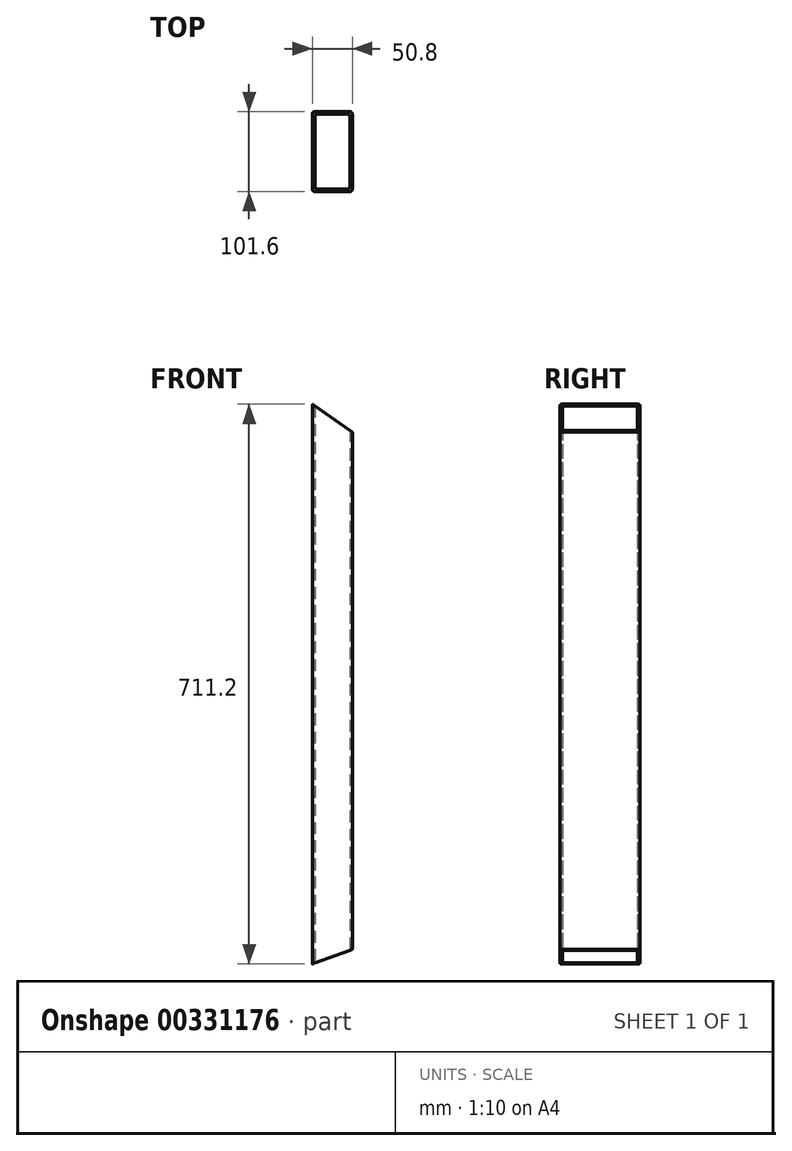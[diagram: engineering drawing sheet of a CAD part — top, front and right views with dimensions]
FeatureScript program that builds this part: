
annotation { "Feature Type Name" : "Feature", "Feature Type Description" : "" }
export const myFeature = defineFeature(function(context is Context, id is Id, definition is map)
    precondition{}
    {
        {
            var Q0;
            Q0=qCreatedBy(makeId("Top.planeOp"),FACE);
            var sketch = newSketch(context, id + "F0", { "sketchPlane" : qUnion([Q0])});
            skLineSegment(sketch, "E0.bottom", {"start": v(22.23, -50.8) * mm, "end": v(-22.22, -50.8) * mm});
            skLineSegment(sketch, "E0.top", {"start": v(22.22, 50.8) * mm, "end": v(-22.23, 50.8) * mm});
            skLineSegment(sketch, "E0.left", {"start": v(25.4, -47.62) * mm, "end": v(25.4, 47.63) * mm});
            skLineSegment(sketch, "E0.right", {"start": v(-25.4, -47.62) * mm, "end": v(-25.4, 47.63) * mm});
            skPoint(sketch, "E0.middle", {"position": v(0, 0) * mm});
            skLineSegment(sketch, "E1.bottom", {"start": v(19.05, -47.62) * mm, "end": v(-19.05, -47.63) * mm});
            skLineSegment(sketch, "E1.top", {"start": v(19.05, 47.63) * mm, "end": v(-19.05, 47.62) * mm});
            skLineSegment(sketch, "E1.left", {"start": v(22.23, -44.45) * mm, "end": v(22.22, 44.45) * mm});
            skLineSegment(sketch, "E1.right", {"start": v(-22.22, -44.45) * mm, "end": v(-22.23, 44.45) * mm});
            skPoint(sketch, "E2.visualSharp", {"position": v(-22.23, 47.62) * mm});
            skArc(sketch, "E2.filletArc", {"start": v(-19.05, 47.62) * mm, "mid": v(-21.3, 46.7) * mm, "end": v(-22.23, 44.45) * mm});
            skPoint(sketch, "E3.visualSharp", {"position": v(-25.4, 50.8) * mm});
            skArc(sketch, "E3.filletArc", {"start": v(-22.23, 50.8) * mm, "mid": v(-24.47, 49.87) * mm, "end": v(-25.4, 47.63) * mm});
            skPoint(sketch, "E4.visualSharp", {"position": v(22.22, 47.63) * mm});
            skArc(sketch, "E4.filletArc", {"start": v(22.22, 44.45) * mm, "mid": v(21.3, 46.7) * mm, "end": v(19.05, 47.63) * mm});
            skPoint(sketch, "E5.visualSharp", {"position": v(25.4, 50.8) * mm});
            skArc(sketch, "E5.filletArc", {"start": v(25.4, 47.63) * mm, "mid": v(24.47, 49.87) * mm, "end": v(22.22, 50.8) * mm});
            skPoint(sketch, "E6.visualSharp", {"position": v(-22.22, -47.63) * mm});
            skArc(sketch, "E6.filletArc", {"start": v(-22.22, -44.45) * mm, "mid": v(-21.3, -46.7) * mm, "end": v(-19.05, -47.63) * mm});
            skPoint(sketch, "E7.visualSharp", {"position": v(22.23, -47.62) * mm});
            skArc(sketch, "E7.filletArc", {"start": v(19.05, -47.62) * mm, "mid": v(21.3, -46.7) * mm, "end": v(22.23, -44.45) * mm});
            skPoint(sketch, "E8.visualSharp", {"position": v(25.4, -50.8) * mm});
            skArc(sketch, "E8.filletArc", {"start": v(22.23, -50.8) * mm, "mid": v(24.47, -49.87) * mm, "end": v(25.4, -47.62) * mm});
            skPoint(sketch, "E9.visualSharp", {"position": v(-25.4, -50.8) * mm});
            skArc(sketch, "E9.filletArc", {"start": v(-25.4, -47.62) * mm, "mid": v(-24.47, -49.87) * mm, "end": v(-22.22, -50.8) * mm});
            skSolve(sketch);
        }
        {
            var Q0;
            Q0 = qSketchRegion(id + "F0", true);
            extrude(context, id + "F1", {"entities" : qUnion([Q0]), "depth" : 711.2 * mm});
        }
        {
            var Q0;
            Q0=qCreatedBy(makeId("Front.planeOp"),FACE);
            var sketch = newSketch(context, id + "F2", { "sketchPlane" : qUnion([Q0])});
            skLineSegment(sketch, "E10", {"start": v(-25.4, 0) * mm, "end": v(25.4, 18.49) * mm});
            skLineSegment(sketch, "E11", {"start": v(25.4, 18.49) * mm, "end": v(25.4, 0) * mm});
            skLineSegment(sketch, "E12", {"start": v(25.4, 0) * mm, "end": v(-25.4, 0) * mm});
            skSolve(sketch);
        }
        {
            var Q0;
            Q0 = qSketchRegion(id + "F2", true);
            extrude(context, id + "F3", {"entities" : qUnion([Q0]), "operationType" : NewBodyOperationType.REMOVE, "endBound" : BoundingType.THROUGH_ALL, "oppositeDirection" : true, "depth" : 25.4 * mm, "hasSecondDirection" : true, "secondDirectionBound" : SecondDirectionBoundingType.THROUGH_ALL, "secondDirectionOppositeDirection" : false, "secondDirectionDepth" : 25.4 * mm});
        }
        {
            var Q0;
            Q0=qCreatedBy(makeId("Front.planeOp"),FACE);
            var sketch = newSketch(context, id + "F4", { "sketchPlane" : qUnion([Q0])});
            skLineSegment(sketch, "E13", {"start": v(-25.4, 711.2) * mm, "end": v(25.4, 675.63) * mm});
            skLineSegment(sketch, "E14", {"start": v(25.4, 675.63) * mm, "end": v(25.4, 711.2) * mm});
            skLineSegment(sketch, "E15", {"start": v(25.4, 711.2) * mm, "end": v(-25.4, 711.2) * mm});
            skSolve(sketch);
        }
        {
            var Q0;
            Q0 = qSketchRegion(id + "F4", true);
            extrude(context, id + "F5", {"entities" : qUnion([Q0]), "operationType" : NewBodyOperationType.REMOVE, "endBound" : BoundingType.THROUGH_ALL, "oppositeDirection" : true, "depth" : 25.4 * mm, "hasSecondDirection" : true, "secondDirectionBound" : SecondDirectionBoundingType.THROUGH_ALL, "secondDirectionOppositeDirection" : false, "secondDirectionDepth" : 25.4 * mm});
        }
    });
